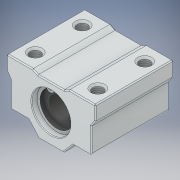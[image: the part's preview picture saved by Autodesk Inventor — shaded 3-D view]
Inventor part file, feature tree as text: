
AUTODESK INVENTOR PART (.ipt)
format: ipt  version: 2019 (Build 230136000, 136)  size: 256,512 bytes
history: mixed  units: in
note: dims shown in document units (in); Inventor stores cm internally (conversion verified against a paired STEP export)
features: thread x4, fillet x1, imported_body x1
ambient origin geometry x8: Origin, YZ Plane, XZ Plane, XY Plane, X Axis, Y Axis, Z Axis, Center Point
bodies: Solid1 (imported_parasolid)
feature tree (6):
  thread  "Thread1"  [1 undecoded]
  thread  "Thread2"  [1 undecoded]
  thread  "Thread3"  [1 undecoded]
  thread  "Thread4"  [1 undecoded]
  fillet  "Redondeo1"  [1 undecoded]
  imported_body  NMx_Import_Brep_tag  [imported B-rep: ~103 faces, bbox_mm=[34.0, 22.0, 30.0]]
note: 5 required parameter values undecoded (feature->parameter linkage not recoverable at this tier; creation-order binding heuristic only, values carry confidence <= 0.55)
